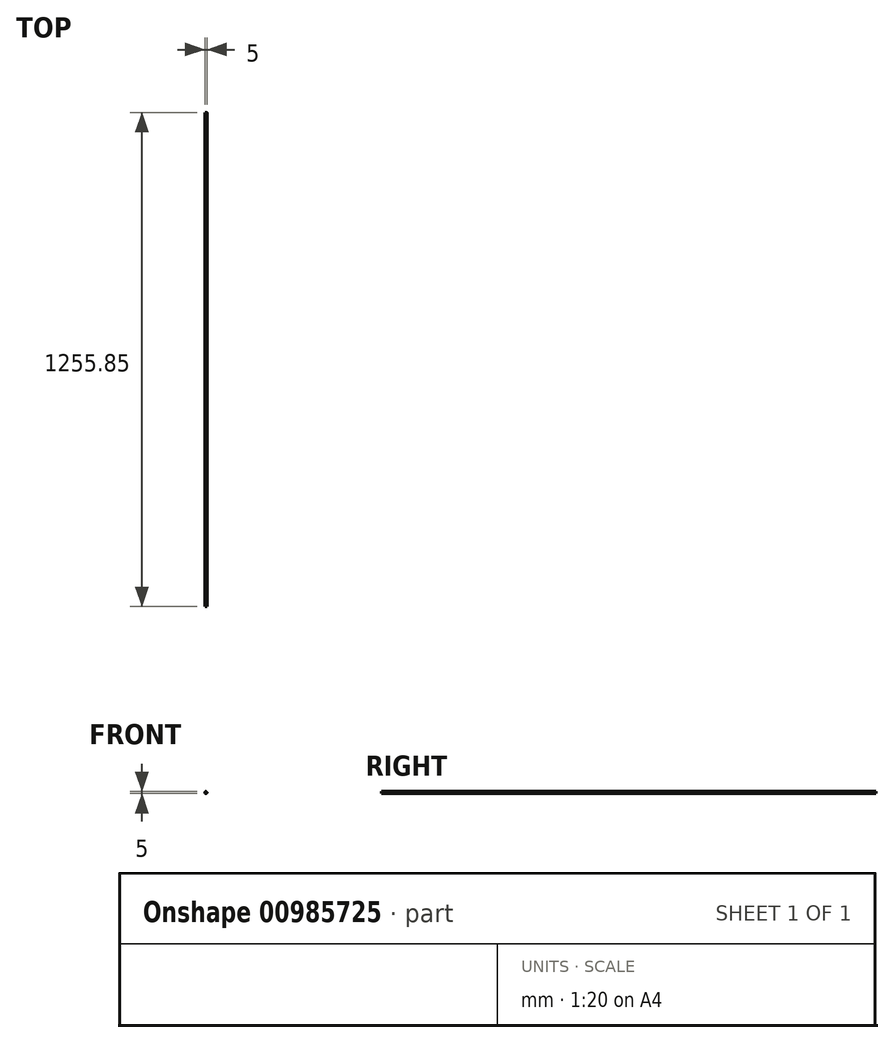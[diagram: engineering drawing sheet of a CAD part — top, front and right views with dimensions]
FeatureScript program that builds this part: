
annotation { "Feature Type Name" : "Feature", "Feature Type Description" : "" }
export const myFeature = defineFeature(function(context is Context, id is Id, definition is map)
    precondition{}
    {
        {
            var Q0;
            Q0=qCreatedBy(makeId("Front.planeOp"),FACE);
            var sketch = newSketch(context, id + "F0", { "sketchPlane" : qUnion([Q0])});
            skCircle(sketch, "E0", {"center": v(-60.55, 41.55) * mm, "radius": 2.5 * mm});
            skSolve(sketch);
        }
        {
            var Q0;
            Q0=makeQuery(id+"F0.imprint","IMPRINT",FACE,{"disambiguationData":[TD([[makeQuery(id+"F0.imprint","IMPRINT",EDGE,{"derivedFrom":sQuery(id+"F0.wireOp",EDGE,"E0")}),1.0]])]});
            extrude(context, id + "F1", {"entities" : qUnion([Q0]), "depth" : 1350 * mm, "offsetDistance" : 25 * mm});
        }
        {
            var Q0;
            Q0=makeQuery(id+"F1.opExtrude","CAP_FACE",FACE,{"disambiguationData":[OSD([sQuery(id+"F0.wireOp",EDGE,"E0")])],"isStart":true});
            extrude(context, id + "F2", {"entities" : qUnion([Q0]), "operationType" : NewBodyOperationType.REMOVE, "oppositeDirection" : true, "depth" : 94.15 * mm, "offsetDistance" : 25 * mm});
        }
    });
